# Revit family: Electronics_Desono_Biamp_Two-Way-High-Coaxial-Surface-Mount-Loudspeaker_DX-S5
name_source: partatom
category: Communication Devices
units: mm (PartAtom-declared; Revit-internal decimal feet)

## family parameters
Cut with Voids When Loaded = No
Host = Face
Maintain Annotation Orientation = No
OmniClass Number = 23.85.10.11.14.14.14
Part Type = Normal
Room Calculation Point = No
Round Connector Dimension = Use Diameter
Shared = No

## types (2) — shared parameters
(Nominal Beamwidth (H x V) = 130° x 125°
Autoformer = 70 V: 60 W, 30 W, 15 W, 7.5 W; 100 V: 60 W, 30 W, 15 W
Certifcations = ETL listed, certifed to CSA STD C22.2# 62368-1
Connector Description = Screw terminal block; 24V 100 W 6Ω
Controls = Wattage / low impedance selector switch
Crossover Frequency = 1.5 kHz
Default Elevation = 4' - 0"
Depth = 0' - 7 1/2"
Description = Desono™ DX-S5 Two-Way High Output Coaxial 5-Inch Surface Mount Loudspeaker
Environmental Rating = IP54 per IEC 60529, IEC 60068-2-5 (Solar Radiation),IEC 60068-2-11 (Salt Mist), IEC 60068-2-42 (SO2),IEC 60068-2-60 (Chlorine)
Height = 0' - 11"
Input Connection = Lever-actuated wire clamping 4-position terminal block with pass-through
Manufacturer = Biamp
Mounting Provisions = ClickMount pan-tilt bracket
Nominal Continuous Power Handling = 24 V (100 W @ 6 Ω)
Nominal Maximum SPL = Peak - 115dB, Continuous - 109dB
Operating Environment = Indoor / Outdoor Direct Exposure
Operating Mode = Single Amplifed with DSP
Operating Range (-10dB) = 75 Hz to 20 kHz
Product Documentation Link = https://downloads.biamp.com
Product Page URL = https://www.biamp.com
Product data url = https://bimobject.com
Rated Continuous Voltage = 15.3 V (24 dBV)
Rated Maximum SPL = Peak - 117dB, Continuous - 105dB
Recommended Amplifers = 100 W - 200 W into 8 Ω, (28 V - 40 V)
Required Accessory = 75 Hz, 12 dB/ oct. high pass flter
Sensitivity = 92 dB (2.83 V); 91 dB (1 W at rated impedance)
Shipping Weight = 11.95 kgf
Transducers = LF 1 x 5 (127 mm) HF 1 x 1 (25 mm) exit compression driver
URL = https://www.biamp.com
Weight = 5.20 kgf
Width = 0' - 7"

## per-type parameters (varying)
| type | Bracket Material | Grill Material | Housing Material |
| DX-S5 W | Biamp - Plastic - White | Biamp - Plastic - White(Grid) | Biamp - Plastic - White |
| DX-S5 B | Biamp - Plastic - Black | Biamp - Plastic - Black(Grid) | Biamp - Plastic - Black |

note: column(s) folded — value = type name in every type: Model

## geometry (parser evidence)
native form markers: Sweep x11
no freeform markers — native parametric forms only
